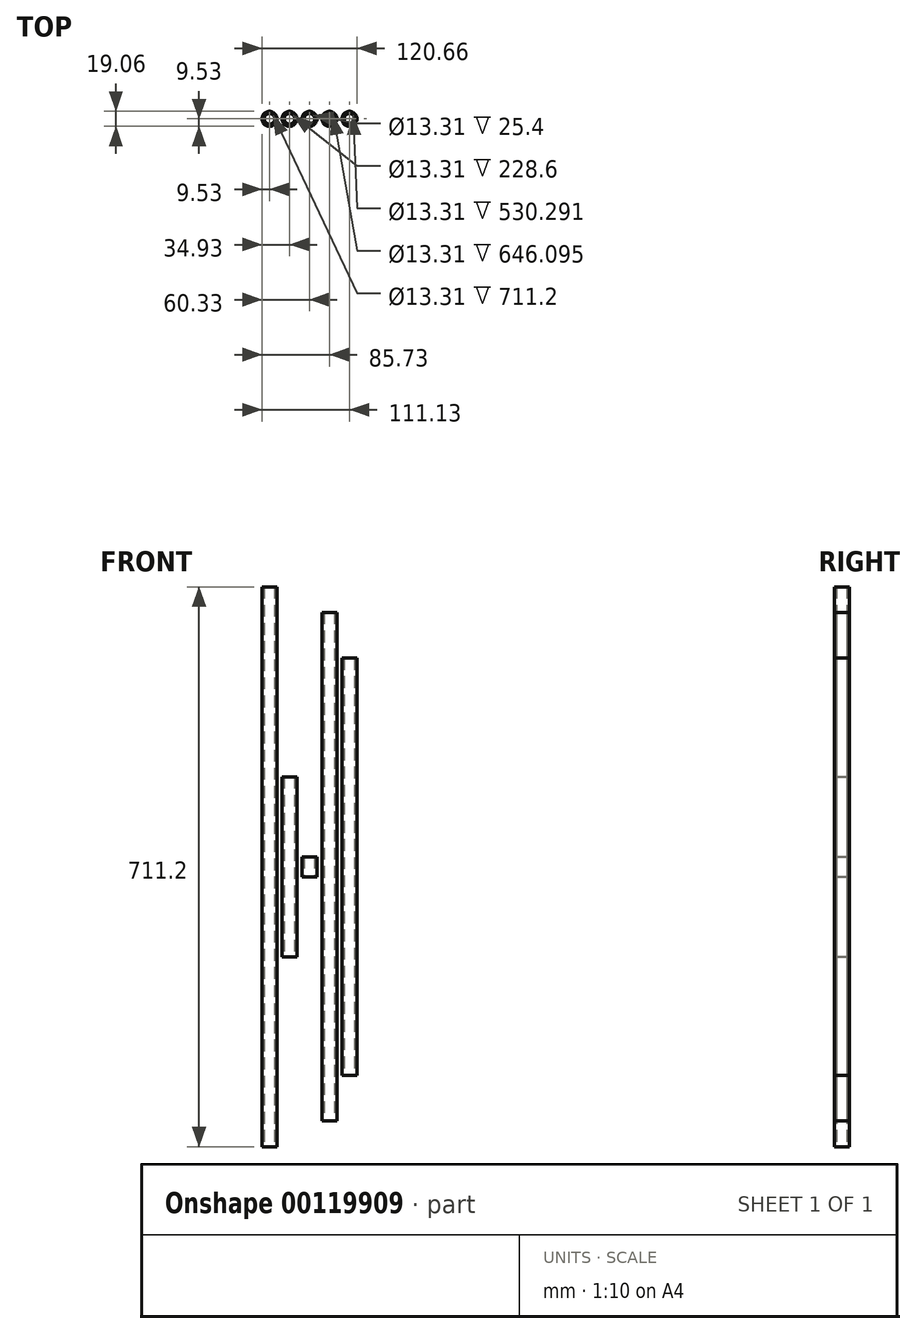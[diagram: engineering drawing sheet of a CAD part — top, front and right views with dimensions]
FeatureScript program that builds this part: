
annotation { "Feature Type Name" : "Feature", "Feature Type Description" : "" }
export const myFeature = defineFeature(function(context is Context, id is Id, definition is map)
    precondition{}
    {
        {
            var Q0;
            Q0=qCreatedBy(makeId("Top.planeOp"),FACE);
            var sketch = newSketch(context, id + "F0", { "sketchPlane" : qUnion([Q0])});
            skCircle(sketch, "E0", {"center": v(0, 0) * mm, "radius": 9.53 * mm});
            skCircle(sketch, "E1.0", {"center": v(0, 0) * mm, "radius": 6.65 * mm});
            skSolve(sketch);
        }
        {
            var Q0;
            Q0 = qSketchRegion(id + "F0", true);
            extrude(context, id + "F1", {"entities" : qUnion([Q0]), "endBound" : BoundingType.SYMMETRIC, "depth" : 711.2 * mm});
        }
        {
            var Q0;
            Q0=qCreatedBy(makeId("Top.planeOp"),FACE);
            var sketch = newSketch(context, id + "F2", { "sketchPlane" : qUnion([Q0])});
            skCircle(sketch, "E2", {"center": v(25.4, 0) * mm, "radius": 6.65 * mm});
            skCircle(sketch, "E3", {"center": v(25.4, 0) * mm, "radius": 9.53 * mm});
            skSolve(sketch);
        }
        {
            var Q0;
            Q0=makeQuery(id+"F2.imprint","IMPRINT",FACE,{"disambiguationData":[TD([[makeQuery(id+"F2.imprint","IMPRINT",EDGE,{"derivedFrom":sQuery(id+"F2.wireOp",EDGE,"E2")}),-1.0]])]});
            extrude(context, id + "F3", {"entities" : qUnion([Q0]), "endBound" : BoundingType.SYMMETRIC, "depth" : 228.6 * mm});
        }
        {
            var Q0;
            Q0=qCreatedBy(makeId("Top.planeOp"),FACE);
            var sketch = newSketch(context, id + "F4", { "sketchPlane" : qUnion([Q0])});
            skCircle(sketch, "E4", {"center": v(50.8, 0) * mm, "radius": 6.65 * mm});
            skCircle(sketch, "E5", {"center": v(50.8, 0) * mm, "radius": 9.53 * mm});
            skSolve(sketch);
        }
        {
            var Q0;
            Q0 = qSketchRegion(id + "F4", true);
            extrude(context, id + "F5", {"entities" : qUnion([Q0]), "endBound" : BoundingType.SYMMETRIC, "depth" : 25.4 * mm});
        }
        {
            var Q0;
            Q0=qCreatedBy(makeId("Top.planeOp"),FACE);
            var sketch = newSketch(context, id + "F6", { "sketchPlane" : qUnion([Q0])});
            skCircle(sketch, "E6", {"center": v(76.2, 0) * mm, "radius": 6.65 * mm});
            skCircle(sketch, "E7", {"center": v(76.2, 0) * mm, "radius": 9.53 * mm});
            skSolve(sketch);
        }
        {
            var Q0;
            Q0 = qSketchRegion(id + "F6", true);
            extrude(context, id + "F7", {"entities" : qUnion([Q0]), "endBound" : BoundingType.SYMMETRIC, "depth" : 646.1 * mm});
        }
        {
            var Q0;
            Q0=qCreatedBy(makeId("Top.planeOp"),FACE);
            var sketch = newSketch(context, id + "F8", { "sketchPlane" : qUnion([Q0])});
            skCircle(sketch, "E8", {"center": v(101.6, 0) * mm, "radius": 6.65 * mm});
            skCircle(sketch, "E9", {"center": v(101.6, 0) * mm, "radius": 9.53 * mm});
            skSolve(sketch);
        }
        {
            var Q0;
            Q0 = qSketchRegion(id + "F8", true);
            extrude(context, id + "F9", {"entities" : qUnion([Q0]), "endBound" : BoundingType.SYMMETRIC, "depth" : 530.3 * mm});
        }
    });
